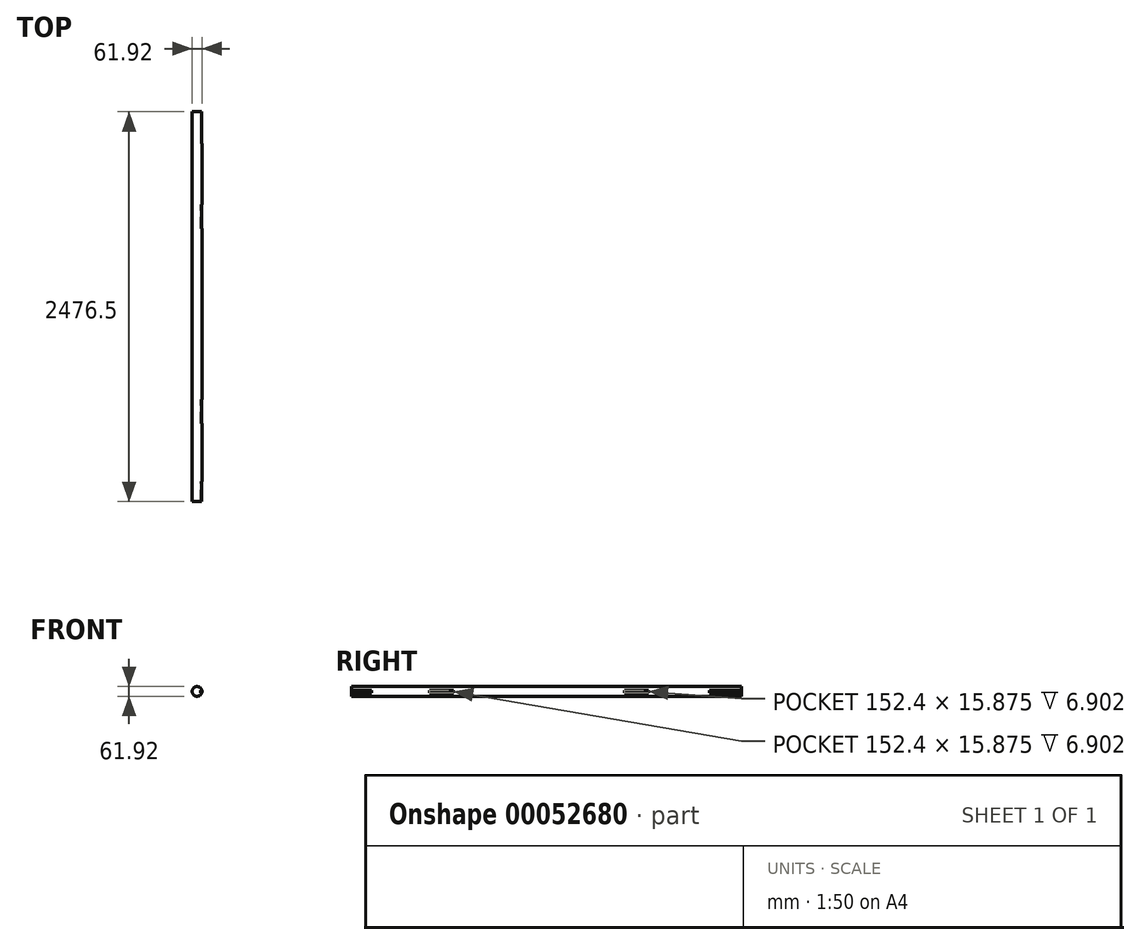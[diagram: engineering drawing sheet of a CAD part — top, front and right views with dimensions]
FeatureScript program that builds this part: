
annotation { "Feature Type Name" : "Feature", "Feature Type Description" : "" }
export const myFeature = defineFeature(function(context is Context, id is Id, definition is map)
    precondition{}
    {
        {
            var Q0;
            Q0=qCreatedBy(makeId("Front.planeOp"),FACE);
            var sketch = newSketch(context, id + "F0", { "sketchPlane" : qUnion([Q0])});
            skCircle(sketch, "E0", {"center": v(0, 0) * mm, "radius": 30.96 * mm});
            skSolve(sketch);
        }
        {
            var Q0;
            Q0=qCreatedBy(makeId("Right.planeOp"),FACE);
            cPlane(context, id + "F1", {"entities" : qUnion([Q0]), "cplaneType" : CPlaneType.OFFSET, "offset" : 30.96 * mm, "width" : 152.4 * mm, "height" : 152.4 * mm});
        }
        {
            var Q0;
            Q0=makeQuery(id+"F0.imprint","IMPRINT",FACE,{"disambiguationData":[TD([[makeQuery(id+"F0.imprint","IMPRINT",EDGE,{"derivedFrom":sQuery(id+"F0.wireOp",EDGE,"E0")}),1.0]])]});
            extrude(context, id + "F2", {"entities" : qUnion([Q0]), "oppositeDirection" : true, "depth" : 2476.5 * mm});
        }
        {
            var Q0;
            Q0=qCreatedBy(id+"F1.planeOp",FACE);
            var sketch = newSketch(context, id + "F3", { "sketchPlane" : qUnion([Q0])});
            skLineSegment(sketch, "E1", {"start": v(0, 0) * mm, "end": v(2883.63, 0) * mm, "construction": true});
            skLineSegment(sketch, "E2.bottom", {"start": v(0, -7.94) * mm, "end": v(127, -7.94) * mm});
            skLineSegment(sketch, "E2.top", {"start": v(0, 7.94) * mm, "end": v(127, 7.94) * mm});
            skLineSegment(sketch, "E2.left", {"start": v(0, -7.94) * mm, "end": v(0, 7.94) * mm});
            skLineSegment(sketch, "E2.right", {"start": v(127, -7.94) * mm, "end": v(127, 7.94) * mm});
            skPoint(sketch, "E2.middle", {"position": v(63.5, 0) * mm});
            skLineSegment(sketch, "E3.bottom", {"start": v(495.3, -7.94) * mm, "end": v(647.7, -7.94) * mm});
            skLineSegment(sketch, "E3.top", {"start": v(495.3, 7.94) * mm, "end": v(647.7, 7.94) * mm});
            skLineSegment(sketch, "E3.left", {"start": v(495.3, -7.94) * mm, "end": v(495.3, 7.94) * mm});
            skLineSegment(sketch, "E3.right", {"start": v(647.7, -7.94) * mm, "end": v(647.7, 7.94) * mm});
            skPoint(sketch, "E3.middle", {"position": v(571.5, 0) * mm});
            skLineSegment(sketch, "E4.bottom", {"start": v(1733.55, -7.94) * mm, "end": v(1885.95, -7.94) * mm});
            skLineSegment(sketch, "E4.top", {"start": v(1733.55, 7.94) * mm, "end": v(1885.95, 7.94) * mm});
            skLineSegment(sketch, "E4.left", {"start": v(1733.55, -7.94) * mm, "end": v(1733.55, 7.94) * mm});
            skLineSegment(sketch, "E4.right", {"start": v(1885.95, -7.94) * mm, "end": v(1885.95, 7.94) * mm});
            skPoint(sketch, "E4.middle", {"position": v(1809.75, 0) * mm});
            skLineSegment(sketch, "E5.bottom", {"start": v(2476.5, -7.94) * mm, "end": v(2273.3, -7.94) * mm});
            skLineSegment(sketch, "E5.top", {"start": v(2476.5, 7.94) * mm, "end": v(2273.3, 7.94) * mm});
            skLineSegment(sketch, "E5.left", {"start": v(2476.5, -7.94) * mm, "end": v(2476.5, 7.94) * mm});
            skLineSegment(sketch, "E5.right", {"start": v(2273.3, -7.94) * mm, "end": v(2273.3, 7.94) * mm});
            skPoint(sketch, "E5.middle", {"position": v(2374.9, 0) * mm});
            skSolve(sketch);
        }
        {
            var Q0;
            Q0 = qSketchRegion(id + "F3", true);
            extrude(context, id + "F4", {"entities" : qUnion([Q0]), "operationType" : NewBodyOperationType.REMOVE, "oppositeDirection" : true, "depth" : 7.94 * mm});
        }
    });
